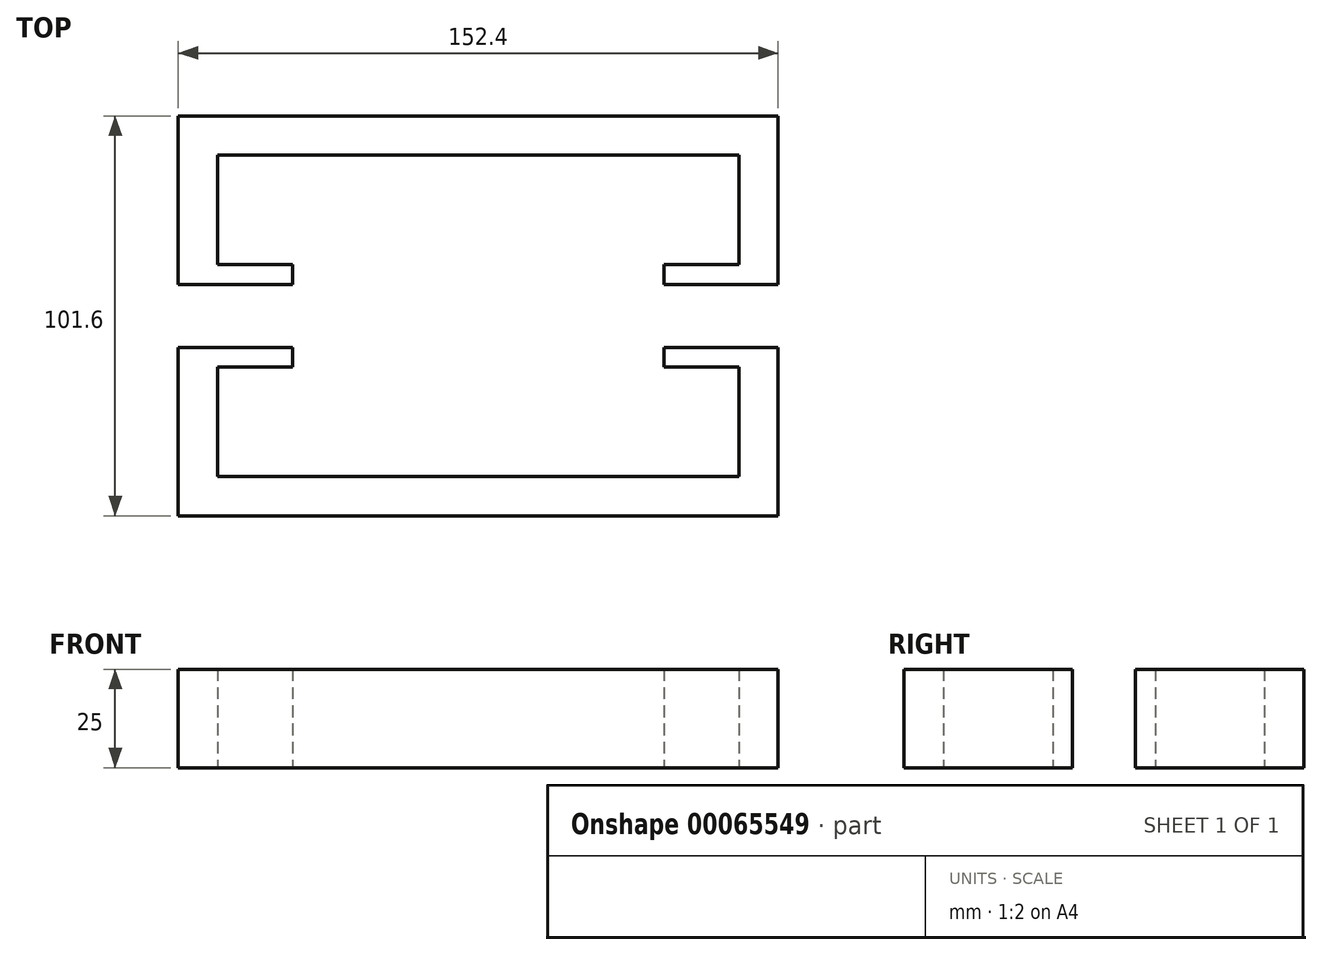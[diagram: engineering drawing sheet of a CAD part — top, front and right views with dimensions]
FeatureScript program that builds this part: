
annotation { "Feature Type Name" : "Feature", "Feature Type Description" : "" }
export const myFeature = defineFeature(function(context is Context, id is Id, definition is map)
    precondition{}
    {
        {
            var Q0;
            Q0=qCreatedBy(makeId("Top.planeOp"),FACE);
            var sketch = newSketch(context, id + "F0", { "sketchPlane" : qUnion([Q0])});
            skLineSegment(sketch, "E0", {"start": v(-76.2, 0) * mm, "end": v(76.2, 0) * mm});
            skLineSegment(sketch, "E1", {"start": v(76.2, 0) * mm, "end": v(76.2, 42.8) * mm});
            skLineSegment(sketch, "E2", {"start": v(-76.2, 0) * mm, "end": v(-76.2, 101.6) * mm});
            skLineSegment(sketch, "E3", {"start": v(76.2, 101.6) * mm, "end": v(-76.2, 101.6) * mm});
            skPoint(sketch, "E4", {"position": v(76.2, 50.8) * mm});
            skPoint(sketch, "E5", {"position": v(-76.2, 50.8) * mm});
            skPoint(sketch, "E6", {"position": v(0, 101.6) * mm});
            skPoint(sketch, "E7", {"position": v(-76.2, 58.8) * mm});
            skPoint(sketch, "E8", {"position": v(-76.2, 42.8) * mm});
            skLineSegment(sketch, "E9", {"start": v(-76.2, 58.8) * mm, "end": v(-76.2, 42.8) * mm});
            skLineSegment(sketch, "E10", {"start": v(-76.2, 58.8) * mm, "end": v(-47.2, 58.8) * mm});
            skLineSegment(sketch, "E11", {"start": v(-76.2, 42.8) * mm, "end": v(-47.2, 42.8) * mm});
            skLineSegment(sketch, "E12", {"start": v(-76.2, 37.8) * mm, "end": v(-47.2, 37.8) * mm});
            skLineSegment(sketch, "E13", {"start": v(-76.2, 63.8) * mm, "end": v(-47.2, 63.8) * mm});
            skLineSegment(sketch, "E14", {"start": v(-47.2, 63.8) * mm, "end": v(-47.2, 58.8) * mm});
            skLineSegment(sketch, "E15", {"start": v(-47.2, 42.8) * mm, "end": v(-47.2, 37.8) * mm});
            skLineSegment(sketch, "E16", {"start": v(-76.2, 63.8) * mm, "end": v(-76.2, 58.8) * mm});
            skLineSegment(sketch, "E17", {"start": v(-76.2, 42.8) * mm, "end": v(-76.2, 37.8) * mm});
            skPoint(sketch, "E18", {"position": v(76.2, 58.8) * mm});
            skPoint(sketch, "E19", {"position": v(76.2, 42.8) * mm});
            skLineSegment(sketch, "E20.trimOffspring", {"start": v(76.2, 58.8) * mm, "end": v(76.2, 101.6) * mm});
            skLineSegment(sketch, "E21", {"start": v(76.2, 42.8) * mm, "end": v(76.2, 58.8) * mm});
            skLineSegment(sketch, "E22", {"start": v(76.2, 42.8) * mm, "end": v(47.2, 42.8) * mm});
            skLineSegment(sketch, "E23", {"start": v(76.2, 37.8) * mm, "end": v(47.2, 37.8) * mm});
            skLineSegment(sketch, "E24", {"start": v(76.2, 58.8) * mm, "end": v(47.2, 58.8) * mm});
            skLineSegment(sketch, "E25", {"start": v(76.2, 63.8) * mm, "end": v(47.2, 63.8) * mm});
            skLineSegment(sketch, "E26", {"start": v(-66.2, 63.8) * mm, "end": v(-66.2, 91.6) * mm});
            skLineSegment(sketch, "E27", {"start": v(-66.2, 37.8) * mm, "end": v(-66.2, 10) * mm});
            skLineSegment(sketch, "E28", {"start": v(-66.2, 10) * mm, "end": v(66.2, 10) * mm});
            skLineSegment(sketch, "E29", {"start": v(66.2, 91.6) * mm, "end": v(66.2, 63.8) * mm});
            skLineSegment(sketch, "E30", {"start": v(66.2, 37.8) * mm, "end": v(66.2, 10) * mm});
            skLineSegment(sketch, "E31", {"start": v(-66.2, 91.6) * mm, "end": v(66.2, 91.6) * mm});
            skPoint(sketch, "E32.orphan", {"position": v(-66.2, 0) * mm});
            skPoint(sketch, "E33.orphan", {"position": v(66.2, 0) * mm});
            skLineSegment(sketch, "E34", {"start": v(47.2, 63.8) * mm, "end": v(47.2, 58.8) * mm});
            skLineSegment(sketch, "E35", {"start": v(47.2, 42.8) * mm, "end": v(47.2, 37.8) * mm});
            skSolve(sketch);
        }
        {
            var Q0;
            {var subQ1=sQuery(id+"F0.wireOp",EDGE,"E3");Q0=makeQuery(id+"F0.imprint","IMPRINT",FACE,{"disambiguationData":[TD([[makeQuery(id+"F0.imprint","IMPRINT",EDGE,{"derivedFrom":subQ1}),1.0]])]});}
            var Q1;
            Q1=makeQuery(id+"F0.imprint","IMPRINT",FACE,{"disambiguationData":[TD([[makeQuery(id+"F0.imprint","IMPRINT",EDGE,{"derivedFrom":sQuery(id+"F0.wireOp",EDGE,"E10")}),1.0]])]});
            var Q2;
            Q2=makeQuery(id+"F0.imprint","IMPRINT",FACE,{"disambiguationData":[TD([[makeQuery(id+"F0.imprint","IMPRINT",EDGE,{"derivedFrom":sQuery(id+"F0.wireOp",EDGE,"E11")}),-1.0]])]});
            var Q3;
            {var subQ4=sQuery(id+"F0.wireOp",EDGE,"E0");Q3=makeQuery(id+"F0.imprint","IMPRINT",FACE,{"disambiguationData":[TD([[makeQuery(id+"F0.imprint","IMPRINT",EDGE,{"derivedFrom":subQ4}),1.0]])]});}
            var Q4;
            {var subQ5=sQuery(id+"F0.wireOp",EDGE,"E24");Q4=makeQuery(id+"F0.imprint","IMPRINT",FACE,{"disambiguationData":[TD([[makeQuery(id+"F0.imprint","IMPRINT",EDGE,{"derivedFrom":subQ5}),-1.0]])]});}
            var Q5;
            {var subQ3=sQuery(id+"F0.wireOp",EDGE,"E22");Q5=makeQuery(id+"F0.imprint","IMPRINT",FACE,{"disambiguationData":[TD([[makeQuery(id+"F0.imprint","IMPRINT",EDGE,{"derivedFrom":subQ3}),1.0]])]});}
            extrude(context, id + "F1", {"entities" : qUnion([Q0, Q1, Q2, Q3, Q4, Q5]), "depth" : 25 * mm});
        }
    });
